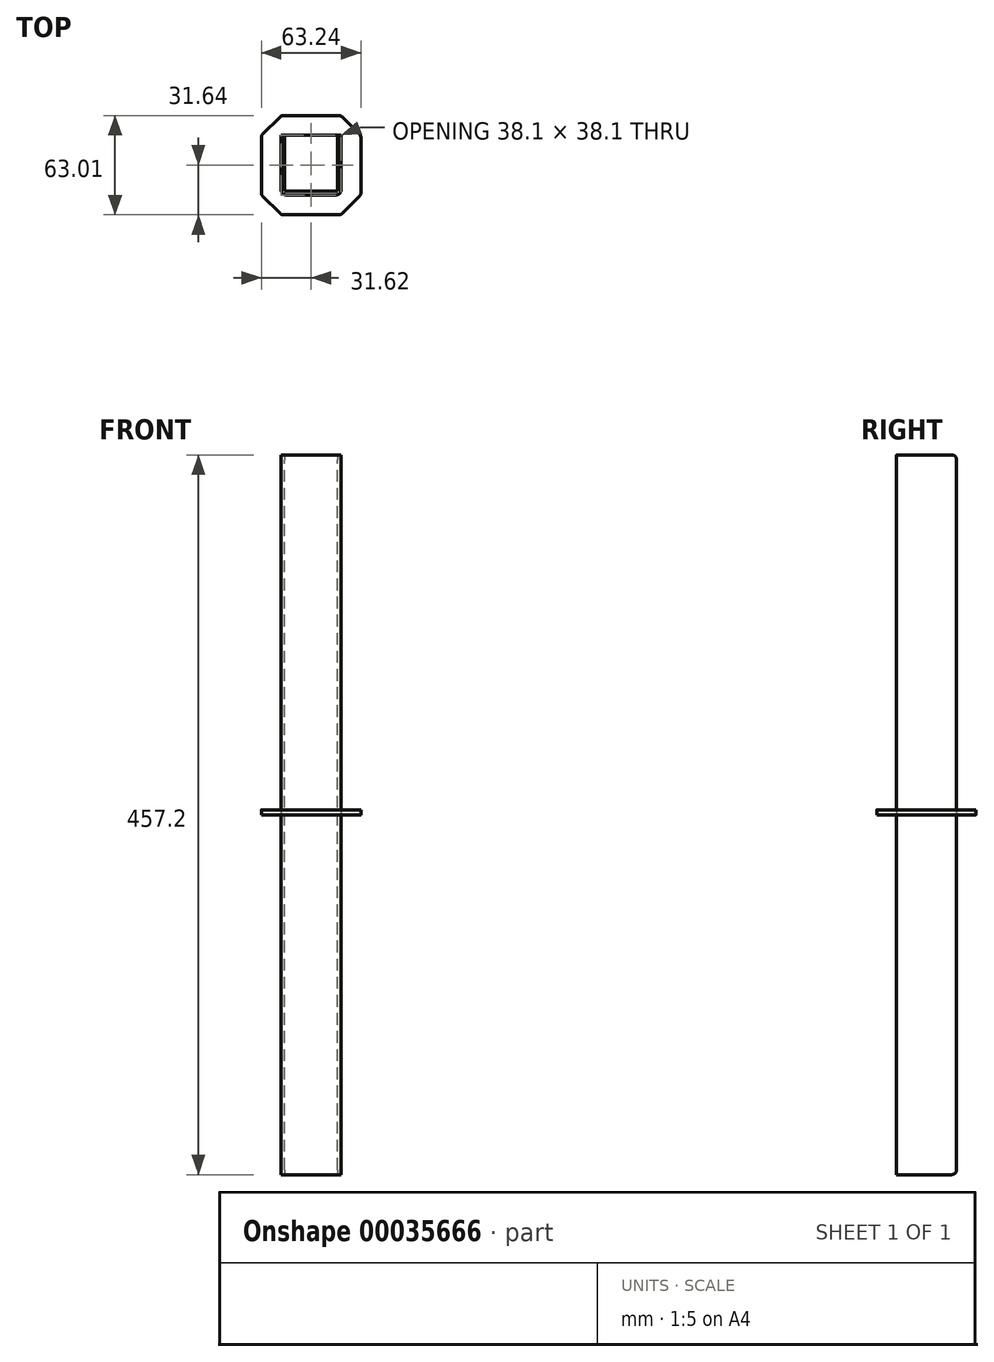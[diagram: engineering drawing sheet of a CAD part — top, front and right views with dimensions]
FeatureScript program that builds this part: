
annotation { "Feature Type Name" : "Feature", "Feature Type Description" : "" }
export const myFeature = defineFeature(function(context is Context, id is Id, definition is map)
    precondition{}
    {
        {
            var Q0;
            Q0=qCreatedBy(makeId("Top.planeOp"),FACE);
            var sketch = newSketch(context, id + "F0", { "sketchPlane" : qUnion([Q0])});
            skLineSegment(sketch, "E0.rect.bottom", {"start": v(-19.05, 19.05) * mm, "end": v(19.05, 19.05) * mm});
            skLineSegment(sketch, "E0.rect.top", {"start": v(-19.05, -19.05) * mm, "end": v(19.05, -19.05) * mm});
            skLineSegment(sketch, "E0.rect.left", {"start": v(-19.05, 19.05) * mm, "end": v(-19.05, -19.05) * mm});
            skLineSegment(sketch, "E0.rect.right", {"start": v(19.05, 19.05) * mm, "end": v(19.05, -19.05) * mm});
            skPoint(sketch, "E0.rect.middle", {"position": v(0, 0) * mm});
            skLineSegment(sketch, "E1.bottom", {"start": v(-16.76, 19.05) * mm, "end": v(16.76, 19.05) * mm});
            skLineSegment(sketch, "E1.top", {"start": v(-16.76, -16.76) * mm, "end": v(16.76, -16.76) * mm});
            skLineSegment(sketch, "E1.left", {"start": v(-16.76, 19.05) * mm, "end": v(-16.76, -16.76) * mm});
            skLineSegment(sketch, "E1.right", {"start": v(16.76, 19.05) * mm, "end": v(16.76, -16.76) * mm});
            skLineSegment(sketch, "E2.bottom", {"start": v(-31.62, 31.37) * mm, "end": v(31.62, 31.37) * mm});
            skLineSegment(sketch, "E2.top", {"start": v(-31.62, -31.64) * mm, "end": v(31.62, -31.64) * mm});
            skLineSegment(sketch, "E2.left", {"start": v(-31.62, 31.37) * mm, "end": v(-31.62, -31.64) * mm});
            skLineSegment(sketch, "E2.right", {"start": v(31.62, 31.37) * mm, "end": v(31.62, -31.64) * mm});
            skLineSegment(sketch, "E3", {"start": v(-16.76, 16.52) * mm, "end": v(16.76, 16.52) * mm});
            skSolve(sketch);
        }
        {
            var Q0;
            Q0=makeQuery(id+"F0.imprint","IMPRINT",FACE,{"disambiguationData":[TD([[makeQuery(id+"F0.imprint","IMPRINT",EDGE,{"derivedFrom":sQuery(id+"F0.wireOp",EDGE,"E0.rect.top")}),1.0]])]});
            extrude(context, id + "F1", {"entities" : qUnion([Q0]), "endBound" : BoundingType.SYMMETRIC, "oppositeDirection" : true, "depth" : 457.2 * mm});
        }
        {
            var Q0;
            Q0=makeQuery(id+"F1.opExtrude","SWEPT_EDGE",EDGE,{"disambiguationData":[OSD([sQuery(id+"F0.wireOp",EDGE,"E0.rect.top"),sQuery(id+"F0.wireOp",EDGE,"E0.rect.right")])]});
            var Q1;
            Q1=makeQuery(id+"F1.opExtrude","SWEPT_EDGE",EDGE,{"disambiguationData":[OSD([sQuery(id+"F0.wireOp",EDGE,"E0.rect.top"),sQuery(id+"F0.wireOp",EDGE,"E0.rect.left")])]});
            fillet(context, id + "F2", {"entities" : qUnion([Q0, Q1]), "radius" : 3.17 * mm, "tangentPropagation" : true, "allowEdgeOverflow" : false});
        }
        {
            var Q0;
            {var subQ0=sQuery(id+"F0.wireOp",EDGE,"E0.rect.bottom");Q0=makeQuery(id+"F1.opExtrude","CAP_EDGE",EDGE,{"disambiguationData":[OSD([subQ0]),TDD([makeQuery(id+"F0.imprint","IMPRINT",EDGE,{"disambiguationData":[TD([[makeQuery(id+"F0.imprint","INTERSECT",VERTEX,{"derivedFrom":[subQ0,sQuery(id+"F0.wireOp",EDGE,"E0.rect.left")]}),-1.0]])],"derivedFrom":subQ0})])],"isStart":true});}
            var Q1;
            {var subQ0=sQuery(id+"F0.wireOp",EDGE,"E0.rect.bottom");Q1=makeQuery(id+"F1.opExtrude","CAP_EDGE",EDGE,{"disambiguationData":[OSD([subQ0]),TDD([makeQuery(id+"F0.imprint","IMPRINT",EDGE,{"disambiguationData":[TD([[makeQuery(id+"F0.imprint","INTERSECT",VERTEX,{"derivedFrom":[subQ0,sQuery(id+"F0.wireOp",EDGE,"E0.rect.right")]}),1.0]])],"derivedFrom":subQ0})])],"isStart":true});}
            var Q2;
            {var subQ0=sQuery(id+"F0.wireOp",EDGE,"E0.rect.bottom");Q2=makeQuery(id+"F1.opExtrude","CAP_EDGE",EDGE,{"disambiguationData":[OSD([subQ0]),TDD([makeQuery(id+"F0.imprint","IMPRINT",EDGE,{"disambiguationData":[TD([[makeQuery(id+"F0.imprint","INTERSECT",VERTEX,{"derivedFrom":[subQ0,sQuery(id+"F0.wireOp",EDGE,"E0.rect.left")]}),-1.0]])],"derivedFrom":subQ0})])],"isStart":false});}
            var Q3;
            {var subQ0=sQuery(id+"F0.wireOp",EDGE,"E0.rect.bottom");Q3=makeQuery(id+"F1.opExtrude","CAP_EDGE",EDGE,{"disambiguationData":[OSD([subQ0]),TDD([makeQuery(id+"F0.imprint","IMPRINT",EDGE,{"disambiguationData":[TD([[makeQuery(id+"F0.imprint","INTERSECT",VERTEX,{"derivedFrom":[subQ0,sQuery(id+"F0.wireOp",EDGE,"E0.rect.right")]}),1.0]])],"derivedFrom":subQ0})])],"isStart":false});}
            fillet(context, id + "F3", {"entities" : qUnion([Q0, Q1, Q2, Q3]), "radius" : 3.17 * mm, "tangentPropagation" : true, "allowEdgeOverflow" : false});
        }
        {
            var Q0;
            Q0=makeQuery(id+"F0.imprint","IMPRINT",FACE,{"disambiguationData":[TD([[makeQuery(id+"F0.imprint","IMPRINT",EDGE,{"derivedFrom":sQuery(id+"F0.wireOp",EDGE,"E0.rect.top")}),-1.0]])]});
            var Q1;
            {var subQ3=sQuery(id+"F0.wireOp",EDGE,"E1.bottom");Q1=makeQuery(id+"F0.imprint","IMPRINT",FACE,{"disambiguationData":[TD([[makeQuery(id+"F0.imprint","IMPRINT",EDGE,{"derivedFrom":subQ3}),-1.0]])]});}
            extrude(context, id + "F4", {"entities" : qUnion([Q0, Q1]), "depth" : 3.17 * mm});
        }
        {
            var Q0;
            Q0=makeQuery(id+"F4.opExtrude","SWEPT_EDGE",EDGE,{"disambiguationData":[OSD([sQuery(id+"F0.wireOp",EDGE,"E2.bottom"),sQuery(id+"F0.wireOp",EDGE,"E2.left")])]});
            var Q1;
            Q1=makeQuery(id+"F4.opExtrude","SWEPT_EDGE",EDGE,{"disambiguationData":[OSD([sQuery(id+"F0.wireOp",EDGE,"E2.top"),sQuery(id+"F0.wireOp",EDGE,"E2.left")])]});
            var Q2;
            Q2=makeQuery(id+"F4.opExtrude","SWEPT_EDGE",EDGE,{"disambiguationData":[OSD([sQuery(id+"F0.wireOp",EDGE,"E2.top"),sQuery(id+"F0.wireOp",EDGE,"E2.right")])]});
            var Q3;
            Q3=makeQuery(id+"F4.opExtrude","SWEPT_EDGE",EDGE,{"disambiguationData":[OSD([sQuery(id+"F0.wireOp",EDGE,"E2.bottom"),sQuery(id+"F0.wireOp",EDGE,"E2.right")])]});
            chamfer(context, id + "F5", {"entities" : qUnion([Q0, Q1, Q2, Q3]), "width" : 12.7 * mm, "tangentPropagation" : true});
        }
        {
            var Q0;
            Q0=makeQuery(id+"F4.opExtrude","SWEPT_EDGE",EDGE,{"disambiguationData":[OSD([sQuery(id+"F0.wireOp",EDGE,"E0.rect.top"),sQuery(id+"F0.wireOp",EDGE,"E0.rect.left")])]});
            var Q1;
            Q1=makeQuery(id+"F4.opExtrude","SWEPT_EDGE",EDGE,{"disambiguationData":[OSD([sQuery(id+"F0.wireOp",EDGE,"E0.rect.top"),sQuery(id+"F0.wireOp",EDGE,"E0.rect.right")])]});
            fillet(context, id + "F6", {"entities" : qUnion([Q0, Q1]), "radius" : 3.17 * mm, "tangentPropagation" : true, "allowEdgeOverflow" : false});
        }
        {
            var Q0;
            {var subQ0=sQuery(id+"F0.wireOp",EDGE,"E2.right");Q0=makeQuery(id+"F5.opChamfer","BLEND_EDGE",EDGE,{"blendedFrom":[makeQuery(id+"F4.opExtrude","SWEPT_EDGE",EDGE,{"disambiguationData":[OSD([sQuery(id+"F0.wireOp",EDGE,"E2.top"),subQ0])]}),makeQuery(id+"F4.opExtrude","SWEPT_FACE",FACE,{"disambiguationData":[OSD([subQ0])]})],"blendedInto":[makeQuery(id+"F4.opExtrude","SWEPT_FACE",FACE,{"disambiguationData":[OSD([subQ0])]})]});}
            var Q1;
            {var subQ0=sQuery(id+"F0.wireOp",EDGE,"E2.right");Q1=makeQuery(id+"F5.opChamfer","BLEND_EDGE",EDGE,{"blendedFrom":[makeQuery(id+"F4.opExtrude","SWEPT_EDGE",EDGE,{"disambiguationData":[OSD([sQuery(id+"F0.wireOp",EDGE,"E2.bottom"),subQ0])]}),makeQuery(id+"F4.opExtrude","SWEPT_FACE",FACE,{"disambiguationData":[OSD([subQ0])]})],"blendedInto":[makeQuery(id+"F4.opExtrude","SWEPT_FACE",FACE,{"disambiguationData":[OSD([subQ0])]})]});}
            var Q2;
            {var subQ0=sQuery(id+"F0.wireOp",EDGE,"E2.bottom");Q2=makeQuery(id+"F5.opChamfer","BLEND_EDGE",EDGE,{"blendedFrom":[makeQuery(id+"F4.opExtrude","SWEPT_EDGE",EDGE,{"disambiguationData":[OSD([subQ0,sQuery(id+"F0.wireOp",EDGE,"E2.right")])]}),makeQuery(id+"F4.opExtrude","SWEPT_FACE",FACE,{"disambiguationData":[OSD([subQ0])]})],"blendedInto":[makeQuery(id+"F4.opExtrude","SWEPT_FACE",FACE,{"disambiguationData":[OSD([subQ0])]})]});}
            var Q3;
            {var subQ0=sQuery(id+"F0.wireOp",EDGE,"E2.bottom");Q3=makeQuery(id+"F5.opChamfer","BLEND_EDGE",EDGE,{"blendedFrom":[makeQuery(id+"F4.opExtrude","SWEPT_EDGE",EDGE,{"disambiguationData":[OSD([subQ0,sQuery(id+"F0.wireOp",EDGE,"E2.left")])]}),makeQuery(id+"F4.opExtrude","SWEPT_FACE",FACE,{"disambiguationData":[OSD([subQ0])]})],"blendedInto":[makeQuery(id+"F4.opExtrude","SWEPT_FACE",FACE,{"disambiguationData":[OSD([subQ0])]})]});}
            var Q4;
            {var subQ0=sQuery(id+"F0.wireOp",EDGE,"E2.top");Q4=makeQuery(id+"F5.opChamfer","BLEND_EDGE",EDGE,{"blendedFrom":[makeQuery(id+"F4.opExtrude","SWEPT_EDGE",EDGE,{"disambiguationData":[OSD([subQ0,sQuery(id+"F0.wireOp",EDGE,"E2.right")])]}),makeQuery(id+"F4.opExtrude","SWEPT_FACE",FACE,{"disambiguationData":[OSD([subQ0])]})],"blendedInto":[makeQuery(id+"F4.opExtrude","SWEPT_FACE",FACE,{"disambiguationData":[OSD([subQ0])]})]});}
            var Q5;
            {var subQ0=sQuery(id+"F0.wireOp",EDGE,"E2.top");Q5=makeQuery(id+"F5.opChamfer","BLEND_EDGE",EDGE,{"blendedFrom":[makeQuery(id+"F4.opExtrude","SWEPT_EDGE",EDGE,{"disambiguationData":[OSD([subQ0,sQuery(id+"F0.wireOp",EDGE,"E2.left")])]}),makeQuery(id+"F4.opExtrude","SWEPT_FACE",FACE,{"disambiguationData":[OSD([subQ0])]})],"blendedInto":[makeQuery(id+"F4.opExtrude","SWEPT_FACE",FACE,{"disambiguationData":[OSD([subQ0])]})]});}
            var Q6;
            {var subQ0=sQuery(id+"F0.wireOp",EDGE,"E2.left");Q6=makeQuery(id+"F5.opChamfer","BLEND_EDGE",EDGE,{"blendedFrom":[makeQuery(id+"F4.opExtrude","SWEPT_EDGE",EDGE,{"disambiguationData":[OSD([sQuery(id+"F0.wireOp",EDGE,"E2.bottom"),subQ0])]}),makeQuery(id+"F4.opExtrude","SWEPT_FACE",FACE,{"disambiguationData":[OSD([subQ0])]})],"blendedInto":[makeQuery(id+"F4.opExtrude","SWEPT_FACE",FACE,{"disambiguationData":[OSD([subQ0])]})]});}
            var Q7;
            {var subQ0=sQuery(id+"F0.wireOp",EDGE,"E2.left");Q7=makeQuery(id+"F5.opChamfer","BLEND_EDGE",EDGE,{"blendedFrom":[makeQuery(id+"F4.opExtrude","SWEPT_EDGE",EDGE,{"disambiguationData":[OSD([sQuery(id+"F0.wireOp",EDGE,"E2.top"),subQ0])]}),makeQuery(id+"F4.opExtrude","SWEPT_FACE",FACE,{"disambiguationData":[OSD([subQ0])]})],"blendedInto":[makeQuery(id+"F4.opExtrude","SWEPT_FACE",FACE,{"disambiguationData":[OSD([subQ0])]})]});}
            fillet(context, id + "F7", {"entities" : qUnion([Q0, Q1, Q2, Q3, Q4, Q5, Q6, Q7]), "radius" : 3.17 * mm, "tangentPropagation" : true, "allowEdgeOverflow" : false});
        }
    });
